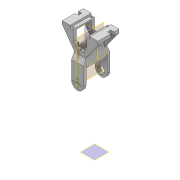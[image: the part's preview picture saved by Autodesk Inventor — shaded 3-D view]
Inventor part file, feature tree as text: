
AUTODESK INVENTOR PART (.ipt)
format: ipt  version: 2018 (Build 220112000, 112)  size: 344,576 bytes
history: native  units: mm
features: extrude x16, sketch x14, plane x4, mirror x4, chamfer x2, fillet x2
ambient origin geometry x8: Origin, YZ Plane, XZ Plane, XY Plane, X Axis, Y Axis, Z Axis, Center Point
bodies: Solid1 (feature_tree)
feature tree (42):
  extrude  "base"  Depth=32.0mm
  extrude  "servo_place"  Depth=11.5mm
  extrude  "screws_servo"  Depth=6.25mm
  plane  "Work Plane1"
  extrude  "pilars_top"  Depth=12.5mm
  extrude  "base_top"  Depth=2.8mm
  extrude  "screw_hole"  Depth=2.8mm
  extrude  "Extrusion11"  Depth=17.0mm TaperAngle=0.0deg
  plane  "Work Plane2"
  extrude  "connector_prev_servo"  Depth=18.0mm
  chamfer  "Chamfer2"  Distance=5.0mm
  fillet  "Fillet3"  Radius=5.0mm
  extrude  "screw_holes"  Depth=2.5mm
  fillet  "Fillet4"  Radius=5.0mm
  extrude  "Extrusion14"  [1 undecoded]
  extrude  "Extrusion16"  Depth=4.0mm
  plane  "Work Plane3"
  plane  "Work Plane4"
  mirror  "Mirror1"
  mirror  "Mirror2"
  extrude  "Extrusion18"  Depth=8.0mm TaperAngle=45.0deg
  extrude  "Extrusion19"  Depth=10.0mm
  extrude  "Extrusion20"  Depth=10.0mm
  mirror  "Mirror3"
  mirror  "Mirror4"
  extrude  "Extrusion21"  Depth=10.0mm
  extrude  "Extrusion22"  Depth=10.0mm TaperAngle=360.0deg
  chamfer  "Chamfer3"  Distance=20.0mm
  sketch  "Sketch1"  dims[d0=18.0mm d1=32.0mm]
  sketch  "Sketch2"  dims[d2=25.0mm d3=0.0mm d4=11.5mm]
  sketch  "Sketch3"  dims[d5=90.0deg d6=6.25mm]
  sketch  "Sketch6"  dims[d7=23.0mm d8=12.5mm]
  sketch  "Sketch9"  dims[d9=18.0mm d10=0.0mm d11=2.8mm]
  sketch  "Sketch12"  dims[d12=2.0mm d13=2.8mm]
  sketch  "Sketch13"  dims[d14=2.0mm d15=17.0mm d16=0.0mm]
  sketch  "Sketch14"  dims[d26=20.0mm d27=0.0mm d39=18.0mm]
  sketch  "Sketch16"  dims[d40=18.0mm d41=5.0mm d42=0.0mm d47=5.0mm d48=0.0mm]
  sketch  "Sketch18"  dims[d55=5.0mm d56=0.0mm d60=2.5mm d61=5.0mm]
  sketch  "Sketch19"  dims[d62=5.0mm d63=-10.0mm]
  sketch  "Sketch20"  dims[d64=4.0mm d65=4.0mm]
  sketch  "Sketch21"  dims[d66=36.0mm d67=0.0mm d68=8.0mm d69=4.0mm d70=45.0deg]
  sketch  "Sketch22"  dims[d71=9.0mm d72=5.5mm d73=6.0mm d74=2.0mm d75=40.0mm d77=360.0deg d79=20.0mm d80=0.0mm d81=9.0mm d82=10.5mm d83=20.0mm d84=0.0mm d95=25.0mm d96=4.6mm d97=0.0mm d98=-16.0mm d99=-9.0mm d100=12.5mm d105=5.0mm d106=10.0mm d107=20.0mm d108=10.0mm d109=0.0mm d110=5.0mm d111=30.0mm d112=3.0mm d113=0.0mm d114=2.5mm d115=2.5mm d116=2.8mm d117=5.0mm d118=0.0mm d119=11.75mm d120=12.5mm d121=23.5mm d122=12.5mm d123=10.0mm d124=0.0mm d125=7.0mm d126=10.0mm d127=0.0mm d128=8.0mm d129=4.0mm d130=45.0deg]
note: 1 required parameter value undecoded (feature->parameter linkage not recoverable at this tier; creation-order binding heuristic only, values carry confidence <= 0.55)
